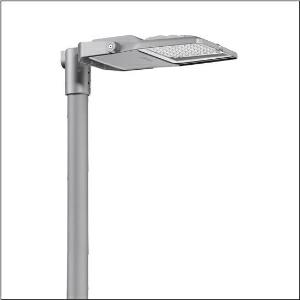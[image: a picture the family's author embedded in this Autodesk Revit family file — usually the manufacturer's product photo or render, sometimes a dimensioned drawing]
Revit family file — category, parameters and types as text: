
# Revit family: floodlight_fl_21_iq_mini___pl61_5xa7771c4c3a_1011
name_source: partatom
category: Lighting Fixtures
units: mm (PartAtom-declared; Revit-internal decimal feet)

## family parameters
Cut with Voids When Loaded = No
Host = Face
Light Source = No
Part Type = Normal
Room Calculation Point = No
Round Connector Dimension = Use Diameter
Shared = No

## types (1)
- --- (1 x LED, 12490 lm, 87.2 W, 4000K)
    Apparent Load = 87 VA
    CIE Flux Codes = 33 65 98 100 100
    Color Rendering = 70
    Color Temperature = 4000K
    Default Elevation = 1800 mm
    Description = Floodlight FL 21 iQ mini, floodlight, primary light control with lens, of PMMA, primary optical cover: protective disc, of toughened safety glass, transparent, light distribution: PL61, light emission: direct distribution, installation type: surface-mounted, LED, High Power LED, rated luminous flux: 12.490lm, luminous efficacy: 143lm/W, light colour: 740, colour temperature: 4000K, control: Auto-Match, Temp-Guard, Lumen-Switch, Night-Set, Smart-Wire, Light-Fading, Desk-Remote (wireless, voltage-free reading and setting of iQ features in the workshop via application-optimized NFC function/RFID function), optimised constant luminous flux control (CLO 2.0), with terminal, 6-pole, mains connection: 220..240V, AC, 50/60Hz, start of lifetime: 87W, end of service life: 92W, reduction: 40W, luminaire housing, of diecast aluminium, powder-coated, Siteco® metallic grey (DB 702S), corrosivity category C5 mid according to DIN EN ISO 12944, sealing non-destructively replaceable, please order mast flange separately, mast bracket, of steel, galvanised, powder-coated, Siteco® metallic grey (DB 702S), protection rating (complete): IP66, insulation class (complete): insulation class II (safety insulation), certification: CE, ENEC, VDE, protection symbol: D, impact resistance: IK08, permissible operating ambient temperature: -40..+40°C, permissible operating ambient temperature for outdoor applications: -40..+50°C, standard: DIN EN 12944, LABS conformity tested according to VDMA 24364:2018-05, packaging unit: 1 piece

Light Distribution: PL61
    Height = 70 mm
    Lamp = 1 x LED
    Lamp Light Flux = 12490 lm
    Lamp Power = 87.2 W
    Lamp count = 1
    Length = 485 mm
    Luminous efficacy = 143 lm/W
    Manufacturer = Siteco
    ModVariant = No
    Model = 5XA7771C4C3A
    Number of Poles = 1
    OnlyDefault = Yes
    Power Factor = 1
    Product Name = Floodlight FL 21 iQ mini | PL61
    Product group = floodlight | pylon annexe
    ProductGroupID = 6200
    Protection Class = Protection class II
    Protection Degree = IP 66
    RLX_Detail_Level = 1
    RLX_Emergency_Light_Flux = 0 lm
    RLX_Emergency_Type = 0
    RLX_Emergency_Type_DB = No
    RlxData = <blob elided: 101313 chars, md5=88eff550>
    Socket = socket
    Standby Power = 0 W
    System Light Flux = 12490 lm
    System Power = 87 W
    Type Comments = factory setting: luminous flux: 100 % | dim-lin: 254 | 456 mA
    Type Image = l_1007125.jpg
    URL = http://relux.com
    VarID = @adj_106263
    Voltage = 0 V
    Weight = 0.00 kg
    Width = 337 mm

## geometry (parser evidence)
native form markers: Blend x4, Sweep x10
no freeform markers — native parametric forms only
